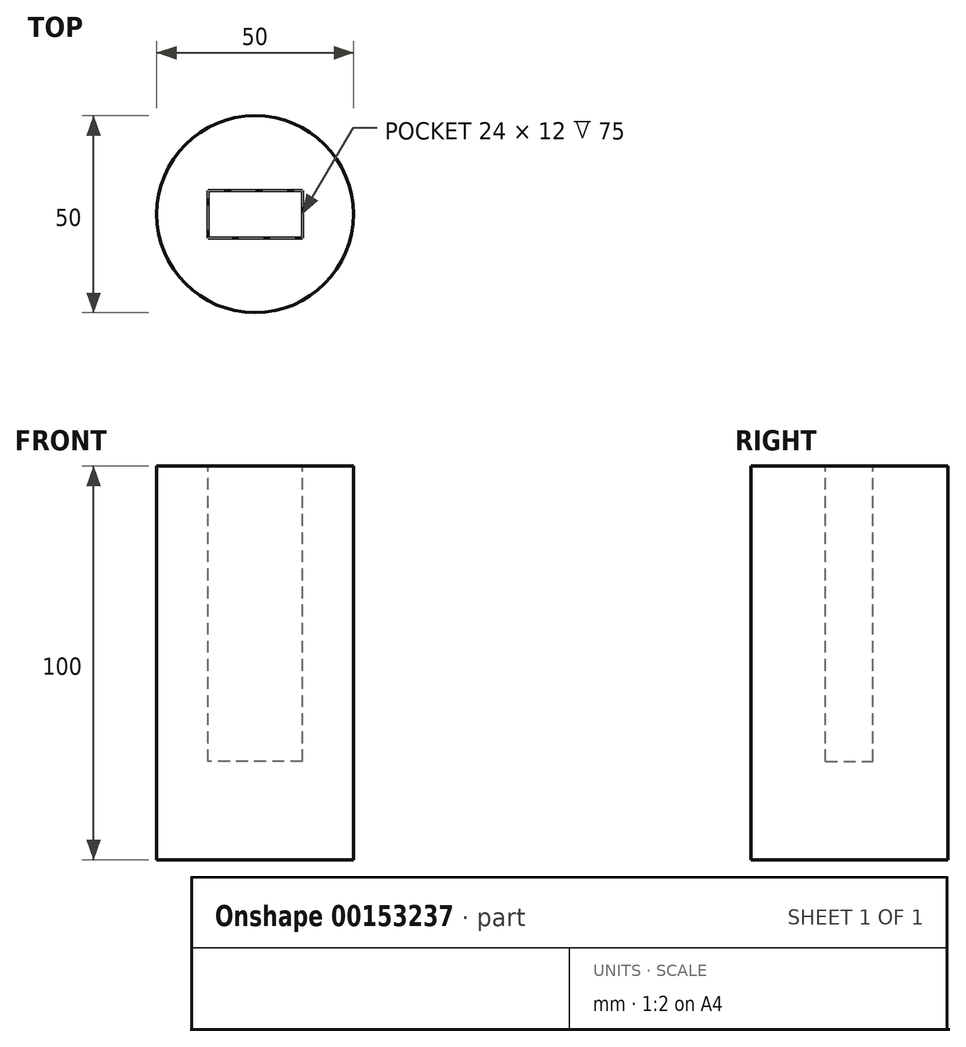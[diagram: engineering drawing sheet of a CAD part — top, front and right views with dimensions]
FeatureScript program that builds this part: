
annotation { "Feature Type Name" : "Feature", "Feature Type Description" : "" }
export const myFeature = defineFeature(function(context is Context, id is Id, definition is map)
    precondition{}
    {
        {
            var Q0;
            Q0=qCreatedBy(makeId("Top.planeOp"),FACE);
            var sketch = newSketch(context, id + "F0", { "sketchPlane" : qUnion([Q0])});
            skCircle(sketch, "E0", {"center": v(0, 0) * mm, "radius": 25 * mm});
            skSolve(sketch);
        }
        {
            var Q0;
            Q0 = qSketchRegion(id + "F0", true);
            extrude(context, id + "F1", {"entities" : qUnion([Q0]), "endBound" : BoundingType.SYMMETRIC, "depth" : 100 * mm});
        }
        {
            var Q0;
            Q0=makeQuery(id+"F1.opExtrude","CAP_FACE",FACE,{"disambiguationData":[OSD([sQuery(id+"F0.wireOp",EDGE,"E0")])],"isStart":false});
            var sketch = newSketch(context, id + "F2", { "sketchPlane" : qUnion([Q0])});
            skLineSegment(sketch, "E1.bottom", {"start": v(12, -6) * mm, "end": v(-12, -6) * mm});
            skLineSegment(sketch, "E1.top", {"start": v(12, 6) * mm, "end": v(-12, 6) * mm});
            skLineSegment(sketch, "E1.left", {"start": v(12, -6) * mm, "end": v(12, 6) * mm});
            skLineSegment(sketch, "E1.right", {"start": v(-12, -6) * mm, "end": v(-12, 6) * mm});
            skPoint(sketch, "E1.middle", {"position": v(0, 0) * mm});
            skSolve(sketch);
        }
        {
            var Q0;
            Q0 = qSketchRegion(id + "F2", true);
            var Q1;
            Q1=makeQuery(id+"F1.opExtrude","CAP_FACE",FACE,{"disambiguationData":[OSD([sQuery(id+"F0.wireOp",EDGE,"E0")])],"isStart":true});
            extrude(context, id + "F3", {"entities" : qUnion([Q0]), "operationType" : NewBodyOperationType.REMOVE, "oppositeDirection" : true, "endBoundEntityFace" : qUnion([Q1]), "depth" : 75 * mm});
        }
    });
